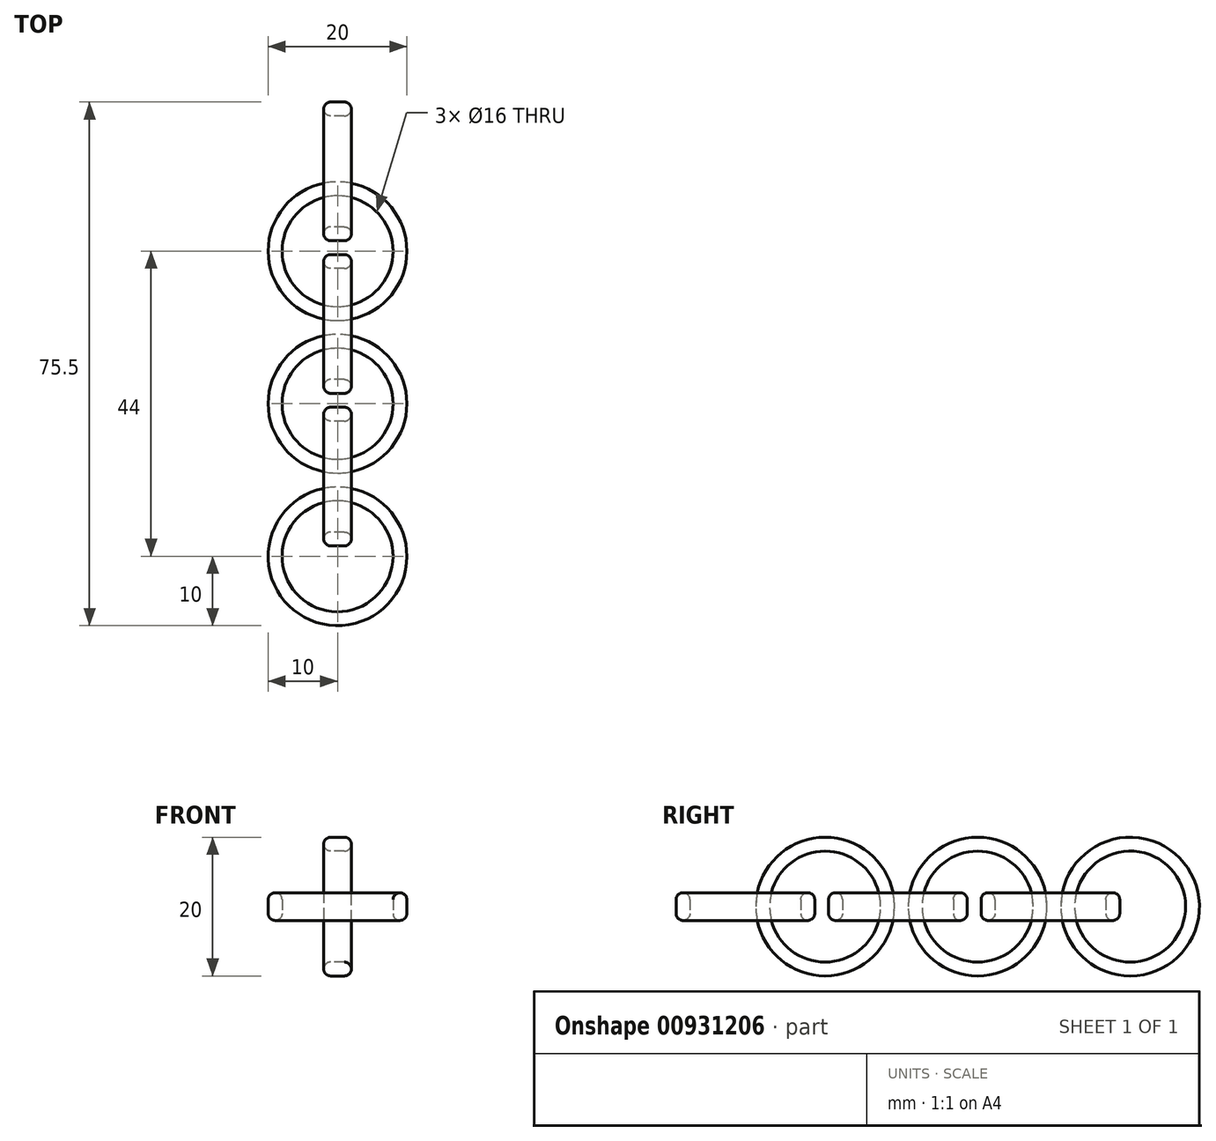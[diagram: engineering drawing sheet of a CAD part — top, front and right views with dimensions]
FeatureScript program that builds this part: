
annotation { "Feature Type Name" : "Feature", "Feature Type Description" : "" }
export const myFeature = defineFeature(function(context is Context, id is Id, definition is map)
    precondition{}
    {
        {
            var Q0;
            Q0=qCreatedBy(makeId("Top.planeOp"),FACE);
            var sketch = newSketch(context, id + "F0", { "sketchPlane" : qUnion([Q0])});
            skCircle(sketch, "E0", {"center": v(0, 0) * mm, "radius": 10 * mm});
            skCircle(sketch, "E1", {"center": v(0, 0) * mm, "radius": 8 * mm});
            skSolve(sketch);
        }
        {
            var Q0;
            Q0=makeQuery(id+"F0.imprint","IMPRINT",FACE,{"disambiguationData":[TD([[makeQuery(id+"F0.imprint","IMPRINT",EDGE,{"derivedFrom":sQuery(id+"F0.wireOp",EDGE,"E0")}),1.0]])]});
            extrude(context, id + "F1", {"entities" : qUnion([Q0]), "endBound" : BoundingType.SYMMETRIC, "depth" : 4 * mm, "offsetDistance" : 25 * mm});
        }
        {
            var Q0;
            Q0=makeQuery(id+"F1.opExtrude","CAP_EDGE",EDGE,{"disambiguationData":[OSD([sQuery(id+"F0.wireOp",EDGE,"E0")])],"isStart":false});
            var Q1;
            Q1=makeQuery(id+"F1.opExtrude","CAP_EDGE",EDGE,{"disambiguationData":[OSD([sQuery(id+"F0.wireOp",EDGE,"E1")])],"isStart":false});
            var Q2;
            Q2=makeQuery(id+"F1.opExtrude","CAP_EDGE",EDGE,{"disambiguationData":[OSD([sQuery(id+"F0.wireOp",EDGE,"E0")])],"isStart":true});
            var Q3;
            Q3=makeQuery(id+"F1.opExtrude","CAP_EDGE",EDGE,{"disambiguationData":[OSD([sQuery(id+"F0.wireOp",EDGE,"E1")])],"isStart":true});
            fillet(context, id + "F2", {"entities" : qUnion([Q0, Q1, Q2, Q3]), "radius" : 1 * mm, "tangentPropagation" : true, "allowEdgeOverflow" : false});
        }
        {
            var Q0;
            Q0=makeQuery(id+"F1.opExtrude","SWEPT_BODY",BODY,{"disambiguationData":[OSD([sQuery(id+"F0.wireOp",EDGE,"E0"),sQuery(id+"F0.wireOp",EDGE,"E1")])]});
            transform(context, id + "F3", {"entities" : qUnion([Q0]), "transformType" : TransformType.TRANSLATION_3D, "dx" : 0 * mm, "dy" : 22 * mm, "dz" : 0 * mm, "makeCopy" : true});
        }
        {
            var Q0;
            Q0=makeQuery(id+"F1.opExtrude","SWEPT_BODY",BODY,{"disambiguationData":[OSD([sQuery(id+"F0.wireOp",EDGE,"E0"),sQuery(id+"F0.wireOp",EDGE,"E1")])]});
            transform(context, id + "F4", {"entities" : qUnion([Q0]), "transformType" : TransformType.TRANSLATION_3D, "dx" : 0 * mm, "dy" : -22 * mm, "dz" : 0 * mm, "makeCopy" : true});
        }
        {
            var Q0;
            Q0=qCreatedBy(makeId("Right.planeOp"),FACE);
            var sketch = newSketch(context, id + "F5", { "sketchPlane" : qUnion([Q0])});
            skCircle(sketch, "E2", {"center": v(-10.5, 0) * mm, "radius": 10 * mm});
            skCircle(sketch, "E3", {"center": v(-10.5, 0) * mm, "radius": 8 * mm});
            skSolve(sketch);
        }
        {
            var Q0;
            Q0=makeQuery(id+"F5.imprint","IMPRINT",FACE,{"disambiguationData":[TD([[makeQuery(id+"F5.imprint","IMPRINT",EDGE,{"derivedFrom":sQuery(id+"F5.wireOp",EDGE,"E2")}),1.0]])]});
            extrude(context, id + "F6", {"entities" : qUnion([Q0]), "endBound" : BoundingType.SYMMETRIC, "depth" : 4 * mm, "offsetDistance" : 25 * mm});
        }
        {
            var Q0;
            Q0=makeQuery(id+"F6.opExtrude","CAP_EDGE",EDGE,{"disambiguationData":[OSD([sQuery(id+"F5.wireOp",EDGE,"E3")])],"isStart":true});
            var Q1;
            Q1=makeQuery(id+"F6.opExtrude","CAP_EDGE",EDGE,{"disambiguationData":[OSD([sQuery(id+"F5.wireOp",EDGE,"E3")])],"isStart":false});
            var Q2;
            Q2=makeQuery(id+"F6.opExtrude","CAP_EDGE",EDGE,{"disambiguationData":[OSD([sQuery(id+"F5.wireOp",EDGE,"E2")])],"isStart":true});
            var Q3;
            Q3=makeQuery(id+"F6.opExtrude","CAP_EDGE",EDGE,{"disambiguationData":[OSD([sQuery(id+"F5.wireOp",EDGE,"E2")])],"isStart":false});
            fillet(context, id + "F7", {"entities" : qUnion([Q0, Q1, Q2, Q3]), "radius" : 1 * mm, "tangentPropagation" : true, "allowEdgeOverflow" : false});
        }
        {
            var Q0;
            Q0=makeQuery(id+"F6.opExtrude","SWEPT_BODY",BODY,{"disambiguationData":[OSD([sQuery(id+"F5.wireOp",EDGE,"E2"),sQuery(id+"F5.wireOp",EDGE,"E3")])]});
            transform(context, id + "F8", {"entities" : qUnion([Q0]), "transformType" : TransformType.TRANSLATION_3D, "dx" : 0 * mm, "dy" : 22 * mm, "dz" : 0 * mm, "makeCopy" : true});
        }
        {
            var Q0;
            Q0=makeQuery(id+"F8.opPattern","COPY",BODY,{"derivedFrom":makeQuery(id+"F6.opExtrude","SWEPT_BODY",BODY,{"disambiguationData":[OSD([sQuery(id+"F5.wireOp",EDGE,"E2"),sQuery(id+"F5.wireOp",EDGE,"E3")])]}),"instanceName":"1"});
            transform(context, id + "F9", {"entities" : qUnion([Q0]), "transformType" : TransformType.TRANSLATION_3D, "dx" : 0 * mm, "dy" : 22 * mm, "dz" : 0 * mm, "makeCopy" : true});
        }
    });
